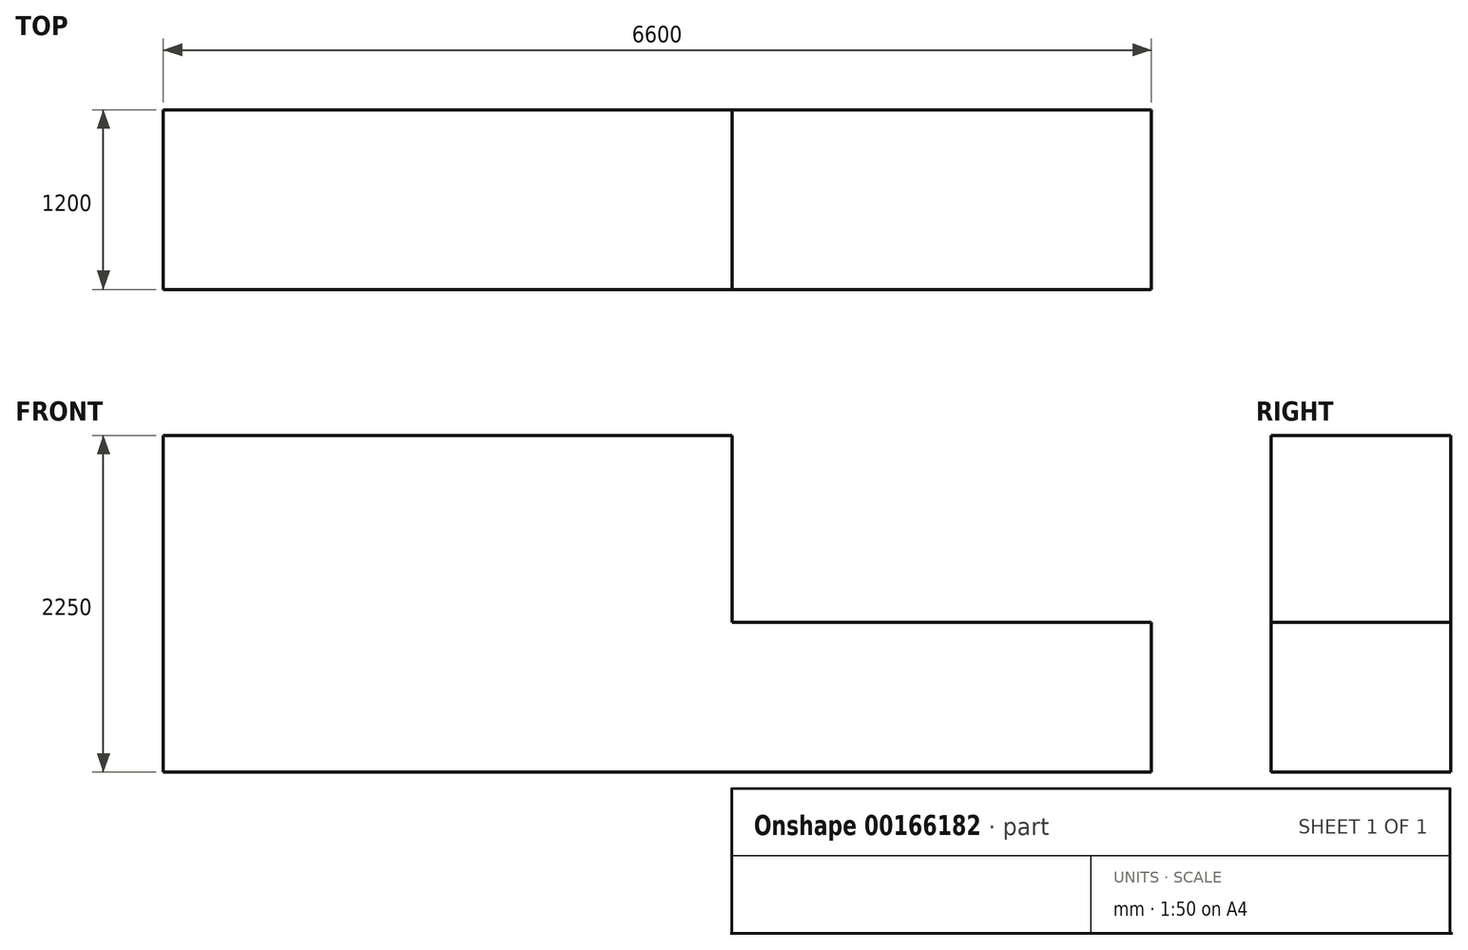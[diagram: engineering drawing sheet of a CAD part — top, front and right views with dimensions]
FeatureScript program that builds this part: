
annotation { "Feature Type Name" : "Feature", "Feature Type Description" : "" }
export const myFeature = defineFeature(function(context is Context, id is Id, definition is map)
    precondition{}
    {
        {
            var Q0;
            Q0=qCreatedBy(makeId("Top.planeOp"),FACE);
            var sketch = newSketch(context, id + "F3", { "sketchPlane" : qUnion([Q0])});
            skLineSegment(sketch, "E0.bottom", {"start": v(3300, -600) * mm, "end": v(-3300, -600) * mm});
            skLineSegment(sketch, "E0.top", {"start": v(3300, 600) * mm, "end": v(-3300, 600) * mm});
            skLineSegment(sketch, "E0.left", {"start": v(3300, -600) * mm, "end": v(3300, 600) * mm});
            skLineSegment(sketch, "E0.right", {"start": v(-3300, -600) * mm, "end": v(-3300, 600) * mm});
            skPoint(sketch, "E0.middle", {"position": v(0, 0) * mm});
            skSolve(sketch);
        }
        {
            var Q0;
            Q0=makeQuery(id+"F3.imprint","IMPRINT",FACE,{"disambiguationData":[TD([[makeQuery(id+"F3.imprint","IMPRINT",EDGE,{"derivedFrom":sQuery(id+"F3.wireOp",EDGE,"E0.bottom")}),-1.0]])]});
            extrude(context, id + "F0", {"entities" : qUnion([Q0]), "depth" : 1000 * mm});
        }
        {
            var Q0;
            Q0=makeQuery(id+"F0.opExtrude","CAP_FACE",FACE,{"disambiguationData":[OSD([sQuery(id+"F3.wireOp",EDGE,"E0.bottom"),sQuery(id+"F3.wireOp",EDGE,"E0.top"),sQuery(id+"F3.wireOp",EDGE,"E0.left"),sQuery(id+"F3.wireOp",EDGE,"E0.right")])],"isStart":false});
            var sketch = newSketch(context, id + "F1", { "sketchPlane" : qUnion([Q0])});
            skLineSegment(sketch, "E1.bottom", {"start": v(-3300, 600) * mm, "end": v(500, 600) * mm});
            skLineSegment(sketch, "E1.top", {"start": v(-3300, -600) * mm, "end": v(500, -600) * mm});
            skLineSegment(sketch, "E1.left", {"start": v(-3300, 600) * mm, "end": v(-3300, -600) * mm});
            skLineSegment(sketch, "E1.right", {"start": v(500, 600) * mm, "end": v(500, -600) * mm});
            skSolve(sketch);
        }
        {
            var Q0;
            Q0=makeQuery(id+"F1.imprint","IMPRINT",FACE,{"disambiguationData":[TD([[makeQuery(id+"F1.imprint","IMPRINT",EDGE,{"derivedFrom":sQuery(id+"F1.wireOp",EDGE,"E1.bottom")}),1.0]])]});
            extrude(context, id + "F2", {"entities" : qUnion([Q0]), "operationType" : NewBodyOperationType.ADD, "depth" : 1250 * mm});
        }
    });
